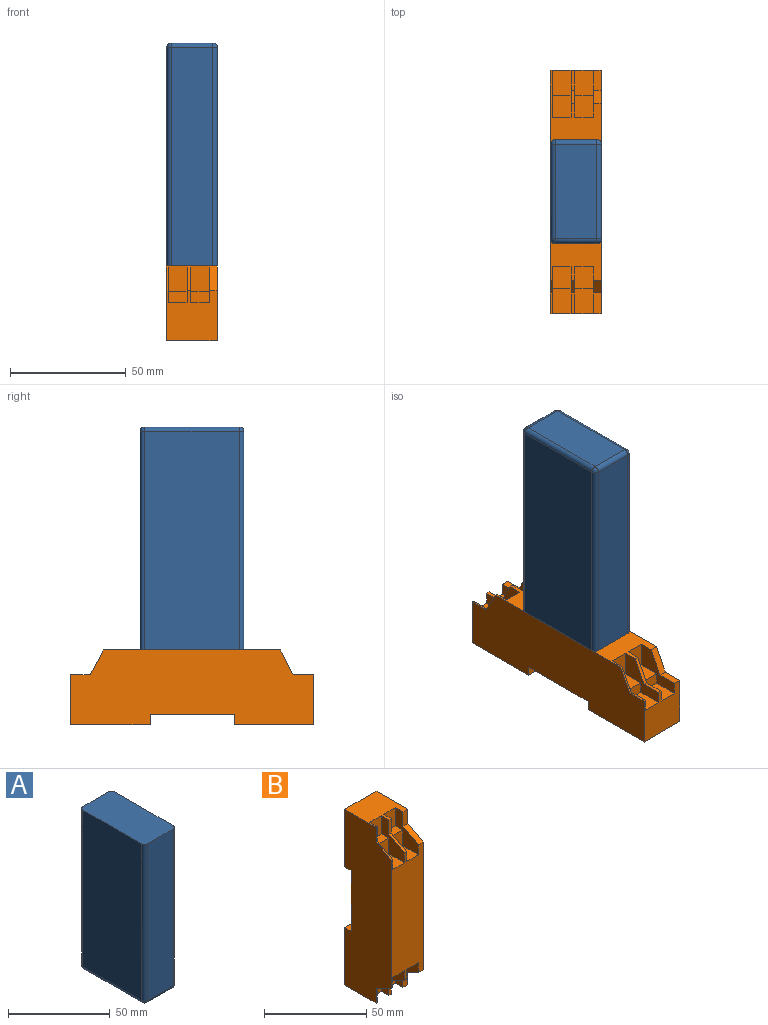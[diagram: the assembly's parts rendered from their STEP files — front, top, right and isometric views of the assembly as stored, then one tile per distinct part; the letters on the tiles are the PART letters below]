
ASSEMBLY  parts=2 mates=1
PART A: 18 faces, bbox 22x45x96.5 mm
  f0: sphere r=2mm, area 5.4mm2, adj f5,f7,f8
  f1: sphere r=2mm, area 5.4mm2, adj f3,f7,f9
  f2: plane 94.5x41mm, normal (1,0,0), area 3874.5mm2, adj f3,f9,f10,f11
  f3: cylinder r=2mm len=94.5mm, axis (0,0,1), area 296.9mm2, adj f1,f2,f4,f11
  f4: plane 94.5x18mm, normal (0,1,0), area 1701mm2, adj f3,f5,f7,f11
  f5: cylinder r=2mm len=94.5mm, axis (0,0,1), area 296.9mm2, adj f0,f4,f6,f11
  f6: plane 94.5x41mm, normal (-1,0,0), area 3874.5mm2, adj f5,f8,f11,f12
  f7: cylinder r=2mm len=18mm, axis (-1,0,0), area 56.5mm2, adj f0,f1,f4,f14
  f8: cylinder r=2mm len=41mm, axis (0,-1,0), area 128.8mm2, adj f0,f6,f13,f14
  f9: cylinder r=2mm len=41mm, axis (0,1,0), area 128.8mm2, adj f1,f2,f14,f15
  f10: cylinder r=2mm len=94.5mm, axis (0,0,1), area 296.9mm2, adj f2,f11,f15,f16
  f11: plane 45x22mm, normal (0,0,1), area 986.6mm2, adj f2,f3,f4,f5,f6,f10,f12,f16
  f12: cylinder r=2mm len=94.5mm, axis (0,0,1), area 296.9mm2, adj f6,f11,f13,f16
  f13: sphere r=2mm, area 5.4mm2, adj f8,f12,f17
  f14: plane 41x18mm, normal (0,0,-1), area 738mm2, adj f7,f8,f9,f17
  f15: sphere r=2mm, area 5.4mm2, adj f9,f10,f17
  f16: plane 94.5x18mm, normal (0,-1,0), area 1701mm2, adj f10,f11,f12,f17
  f17: cylinder r=2mm len=18mm, axis (1,0,0), area 56.5mm2, adj f13,f14,f15,f16
PART B: 46 faces, bbox 21.9x32.4x105.3 mm
  f0: plane 8.11x5mm, normal (0,0,1), area 40.6mm2, adj f1,f10,f17,f19
  f1: plane 9.4x8.11mm, normal (0,-1,0), area 76.3mm2, adj f0,f17,f18,f19
  f2: plane 8.11x5mm, normal (0,0,1), area 40.6mm2, adj f3,f8,f21,f23
  f3: plane 9.4x8.11mm, normal (0,-1,0), area 76.3mm2, adj f2,f21,f22,f23
  f4: plane 9.4x8.11mm, normal (0,-1,0), area 76.3mm2, adj f5,f14,f25,f27
  f5: plane 8.11x5mm, normal (0,0,-1), area 40.6mm2, adj f4,f25,f26,f27
  f6: plane 9.4x8.11mm, normal (0,-1,0), area 76.3mm2, adj f7,f12,f29,f31
  f7: plane 8.11x5mm, normal (0,0,-1), area 40.6mm2, adj f6,f29,f30,f31
  f8: plane 10.93x8.11mm, normal (0,-1,0), area 88.7mm2, adj f2,f21,f23,f37
  f9: plane 8.64x1.59mm, normal (0,-1,0), area 13.7mm2, adj f19,f20,f21,f37
  f10: plane 10.93x8.11mm, normal (0,-1,0), area 88.7mm2, adj f0,f17,f19,f37
  f11: plane 8.64x3.33mm, normal (0,-1,0), area 28.7mm2, adj f16,f17,f32,f37
  f12: plane 11x8.11mm, normal (0,0,-1), area 89.2mm2, adj f6,f29,f31,f40
  f13: plane 10.77x5.45mm, normal (0,-0.45,-0.89), area 19.2mm2, adj f27,f28,f29,f40
  f14: plane 11x8.11mm, normal (0,0,-1), area 89.2mm2, adj f4,f25,f27,f40
  f15: plane 10.77x5.45mm, normal (0,-0.45,-0.89), area 40.1mm2, adj f24,f25,f32,f40
  f16: plane 10.77x5.72mm, normal (0,-0.47,0.88), area 40.5mm2, adj f11,f17,f32,f40
  f17: plane 20.33x16mm, normal (-1,0,0), area 154.5mm2, adj f0,f1,f10,f11,f16,f18,f37,f40
  f18: plane 11x8.11mm, normal (0,0,1), area 89.2mm2, adj f1,f17,f19,f40
  f19: plane 20.33x16mm, normal (1,0,0), area 154.5mm2, adj f0,f1,f9,f10,f18,f20,f37,f40
  f20: plane 10.77x5.72mm, normal (0,-0.47,0.88), area 19.4mm2, adj f9,f19,f21,f40
  f21: plane 20.33x16mm, normal (-1,0,0), area 154.5mm2, adj f2,f3,f8,f9,f20,f22,f37,f40
  f22: plane 11x8.11mm, normal (0,0,1), area 89.2mm2, adj f3,f21,f23,f40
  f23: plane 20.33x16mm, normal (1,0,0), area 154.5mm2, adj f2,f3,f8,f22,f37,f38,f39,f40
  f24: plane 8.91x3.33mm, normal (0,-1,0), area 29.6mm2, adj f15,f25,f32,f43
  f25: plane 20.33x16mm, normal (-1,0,0), area 153mm2, adj f4,f5,f14,f15,f24,f26,f40,f43
  f26: plane 10.93x8.11mm, normal (0,-1,0), area 88.7mm2, adj f5,f25,f27,f43
  f27: plane 20.33x16mm, normal (1,0,0), area 153mm2, adj f4,f5,f13,f14,f26,f28,f40,f43
  f28: plane 8.91x1.59mm, normal (0,-1,0), area 14.1mm2, adj f13,f27,f29,f43
  f29: plane 20.33x16mm, normal (-1,0,0), area 153mm2, adj f6,f7,f12,f13,f28,f30,f40,f43
  f30: plane 10.93x8.11mm, normal (0,-1,0), area 88.7mm2, adj f7,f29,f31,f43
  f31: plane 20.33x16mm, normal (1,0,0), area 153mm2, adj f6,f7,f12,f30,f40,f41,f42,f43
  f32: plane 105.3x32.44mm, normal (1,0,0), area 3006.7mm2, adj f11,f15,f16,f24,f33,f34,f35,f36
  f33: plane 21.93x4.39mm, normal (0,0,1), area 96.2mm2, adj f32,f34,f44,f45
  f34: plane 36.45x21.93mm, normal (0,1,0), area 799.4mm2, adj f32,f33,f35,f45
  f35: plane 21.93x4.39mm, normal (0,0,-1), area 96.2mm2, adj f32,f34,f36,f45
  f36: plane 34.55x21.93mm, normal (0,1,0), area 757.6mm2, adj f32,f35,f37,f45
  f37: plane 21.93x21.67mm, normal (0,0,1), area 390.4mm2, adj f8,f9,f10,f11,f17,f19,f21,f23
  f38: plane 8.64x0.79mm, normal (0,-1,0), area 6.9mm2, adj f23,f37,f39,f45
  f39: plane 10.77x5.72mm, normal (0,-0.47,0.88), area 9.7mm2, adj f23,f38,f40,f45
  f40: plane 76.58x21.93mm, normal (0,-1,0), area 1485.7mm2, adj f12,f13,f14,f15,f16,f17,f18,f19
  f41: plane 10.77x5.45mm, normal (0,-0.45,-0.89), area 9.6mm2, adj f31,f40,f42,f45
  f42: plane 8.91x0.79mm, normal (0,-1,0), area 7.1mm2, adj f31,f41,f43,f45
  f43: plane 21.93x21.67mm, normal (0,0,-1), area 390.4mm2, adj f24,f25,f26,f27,f28,f29,f30,f31
  f44: plane 34.3x21.93mm, normal (0,1,0), area 752.3mm2, adj f32,f33,f43,f45
  f45: plane 105.3x32.44mm, normal (-1,0,0), area 3006.7mm2, adj f33,f34,f35,f36,f37,f38,f39,f40
PLACE A rot(axis=(1,0,0),180deg) t=(50.79,41.1,124.55)mm
PLACE B rot(axis=(-1,0,0),90deg) t=(-32.03,-95.24,5.75)mm fixed
MATE fastened B.f40 <-> A.f11  axis (0,0,1) through (0.17,0.12,28.05)mm
